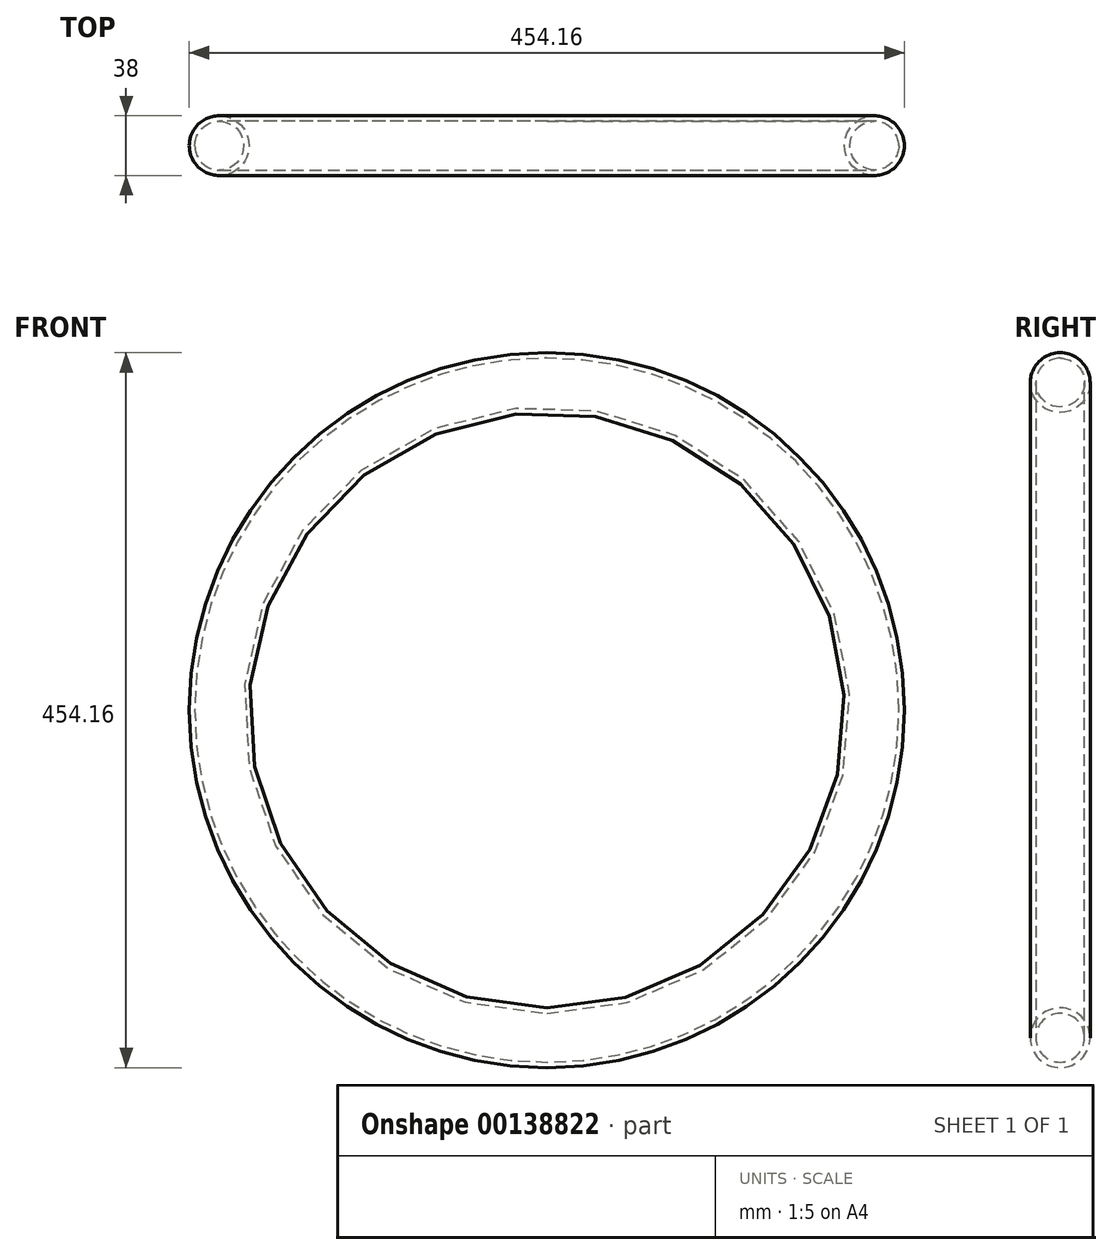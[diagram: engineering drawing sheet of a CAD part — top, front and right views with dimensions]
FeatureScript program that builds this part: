
annotation { "Feature Type Name" : "Feature", "Feature Type Description" : "" }
export const myFeature = defineFeature(function(context is Context, id is Id, definition is map)
    precondition{}
    {
        {
            var Q0;
            Q0=qCreatedBy(makeId("Front.planeOp"),FACE);
            var sketch = newSketch(context, id + "F0", { "sketchPlane" : qUnion([Q0])});
            skLineSegment(sketch, "E0.bottom", {"start": v(62.5, 12.5) * mm, "end": v(-62.5, 12.5) * mm, "construction": true});
            skLineSegment(sketch, "E0.top", {"start": v(62.5, -12.5) * mm, "end": v(-62.5, -12.5) * mm});
            skLineSegment(sketch, "E0.left", {"start": v(62.5, 12.5) * mm, "end": v(62.5, -12.5) * mm, "construction": true});
            skLineSegment(sketch, "E0.right", {"start": v(-62.5, 12.5) * mm, "end": v(-62.5, -12.5) * mm, "construction": true});
            skPoint(sketch, "E0.middle", {"position": v(0, 0) * mm});
            skPoint(sketch, "E1", {"position": v(-62.5, 12.5) * mm});
            skPoint(sketch, "E2", {"position": v(62.5, 12.5) * mm});
            skPoint(sketch, "E3", {"position": v(0, -12.5) * mm});
            skLineSegment(sketch, "E4", {"start": v(0, 187.5) * mm, "end": v(-62.5, -12.5) * mm});
            skLineSegment(sketch, "E5", {"start": v(-67.27, -0.85) * mm, "end": v(0, 187.5) * mm});
            skCircle(sketch, "E6", {"center": v(0, 187.5) * mm, "radius": 200 * mm});
            skSolve(sketch);
        }
        {
            var Q0;
            Q0=qCreatedBy(makeId("Right.planeOp"),FACE);
            var Q1;
            Q1=sQuery(id+"F0.wireOp",VERTEX,"E1");
            cPlane(context, id + "F1", {"entities" : qUnion([Q0, Q1]), "cplaneType" : CPlaneType.PLANE_POINT, "offset" : 25 * mm, "width" : 150 * mm, "height" : 150 * mm});
        }
        {
            var Q0;
            Q0=qCreatedBy(id+"F1.planeOp",FACE);
            var Q1;
            Q1=sQuery(id+"F0.wireOp",EDGE,"E5");
            cPlane(context, id + "F2", {"entities" : qUnion([Q0, Q1]), "cplaneType" : CPlaneType.LINE_ANGLE, "offset" : 25 * mm, "angle" : 0 * degree, "width" : 150 * mm, "height" : 150 * mm});
        }
        {
            var Q0;
            Q0=qCreatedBy(id+"F2.planeOp",FACE);
            var sketch = newSketch(context, id + "F3", { "sketchPlane" : qUnion([Q0])});
            skCircle(sketch, "E7", {"center": v(0, -31.5) * mm, "radius": 19 * mm});
            skCircle(sketch, "E8", {"center": v(0, -31.5) * mm, "radius": 15.5 * mm});
            skSolve(sketch);
        }
        {
            var Q0;
            Q0=makeQuery(id+"F3.imprint","IMPRINT",FACE,{"disambiguationData":[TD([[makeQuery(id+"F3.imprint","IMPRINT",EDGE,{"derivedFrom":sQuery(id+"F3.wireOp",EDGE,"E7")}),1.0]])]});
            var Q1;
            Q1=sQuery(id+"F0.wireOp",EDGE,"E6");
            sweep(context, id + "F4", {"profiles" : qUnion([Q0]), "path" : qUnion([Q1])});
        }
    });
